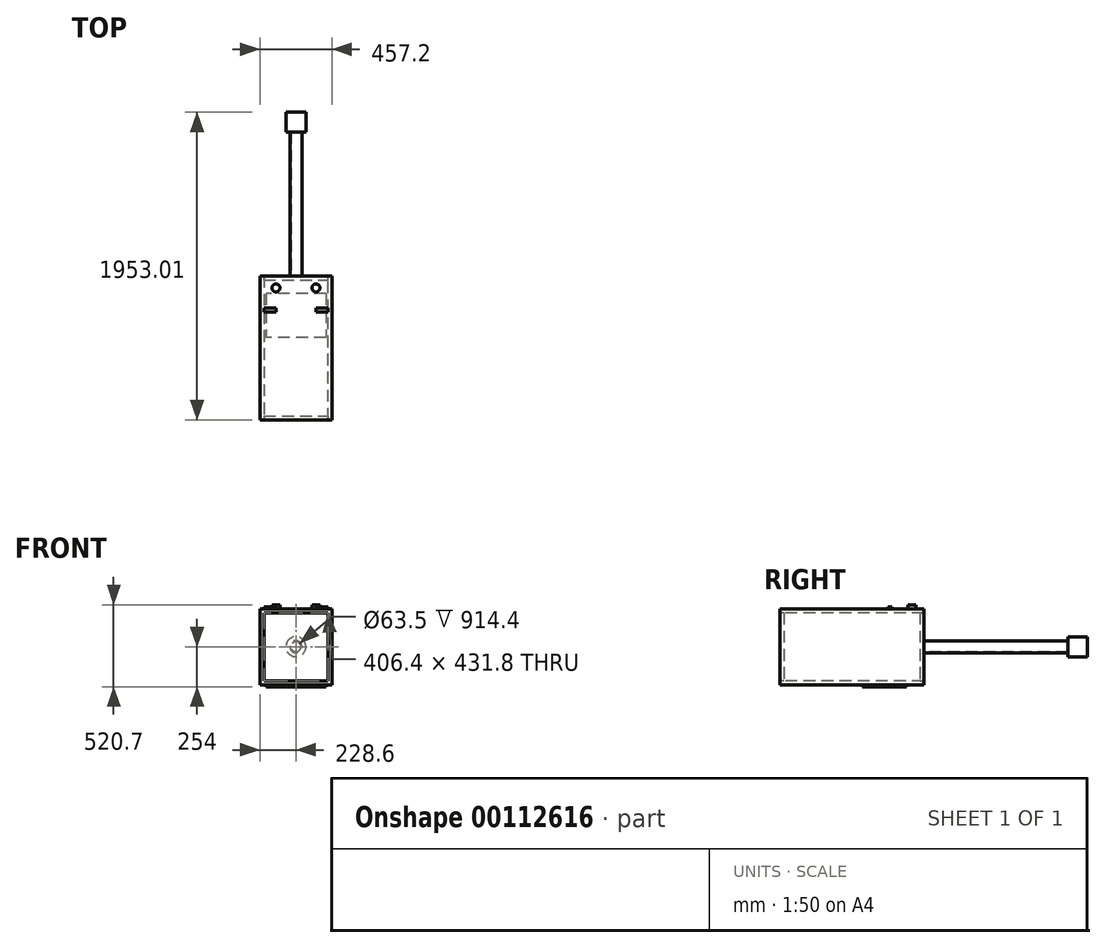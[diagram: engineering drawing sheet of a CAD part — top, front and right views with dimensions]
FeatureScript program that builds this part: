
annotation { "Feature Type Name" : "Feature", "Feature Type Description" : "" }
export const myFeature = defineFeature(function(context is Context, id is Id, definition is map)
    precondition{}
    {
        {
            var Q0;
            Q0=qCreatedBy(makeId("Top.planeOp"),FACE);
            var sketch = newSketch(context, id + "F0", { "sketchPlane" : qUnion([Q0])});
            skLineSegment(sketch, "E0", {"start": v(-228.6, 0) * mm, "end": v(228.6, 0) * mm});
            skLineSegment(sketch, "E1", {"start": v(228.6, 0) * mm, "end": v(228.6, 914.4) * mm});
            skLineSegment(sketch, "E2", {"start": v(228.6, 914.4) * mm, "end": v(-228.6, 914.4) * mm});
            skLineSegment(sketch, "E3", {"start": v(-228.6, 914.4) * mm, "end": v(-228.6, 0) * mm});
            skPoint(sketch, "E4", {"position": v(228.6, 457.2) * mm});
            skSolve(sketch);
        }
        {
            var Q0;
            Q0=makeQuery(id+"F0.imprint","IMPRINT",FACE,{"disambiguationData":[TD([[makeQuery(id+"F0.imprint","IMPRINT",EDGE,{"derivedFrom":sQuery(id+"F0.wireOp",EDGE,"E0")}),1.0]])]});
            extrude(context, id + "F1", {"entities" : qUnion([Q0]), "depth" : 25.4 * mm});
        }
        {
            var Q0;
            Q0=makeQuery(id+"F1.opExtrude","CAP_FACE",FACE,{"disambiguationData":[OSD([sQuery(id+"F0.wireOp",EDGE,"E0"),sQuery(id+"F0.wireOp",EDGE,"E1"),sQuery(id+"F0.wireOp",EDGE,"E2"),sQuery(id+"F0.wireOp",EDGE,"E3")])],"isStart":false});
            var sketch = newSketch(context, id + "F2", { "sketchPlane" : qUnion([Q0])});
            skLineSegment(sketch, "E5", {"start": v(-228.6, 914.4) * mm, "end": v(-228.6, 0) * mm});
            skLineSegment(sketch, "E6", {"start": v(-203.2, 914.4) * mm, "end": v(-203.2, 0) * mm});
            skLineSegment(sketch, "E7", {"start": v(-228.6, 914.4) * mm, "end": v(-203.2, 914.4) * mm});
            skLineSegment(sketch, "E8", {"start": v(-228.6, 0) * mm, "end": v(-203.2, 0) * mm});
            skSolve(sketch);
        }
        {
            var Q0;
            Q0=makeQuery(id+"F2.imprint","IMPRINT",FACE,{"disambiguationData":[TD([[makeQuery(id+"F2.imprint","IMPRINT",EDGE,{"derivedFrom":sQuery(id+"F2.wireOp",EDGE,"E5")}),1.0]])]});
            extrude(context, id + "F3", {"entities" : qUnion([Q0]), "operationType" : NewBodyOperationType.ADD, "depth" : 457.2 * mm});
        }
        {
            var Q0;
            Q0=makeQuery(id+"F1.opExtrude","CAP_FACE",FACE,{"disambiguationData":[OSD([sQuery(id+"F0.wireOp",EDGE,"E0"),sQuery(id+"F0.wireOp",EDGE,"E1"),sQuery(id+"F0.wireOp",EDGE,"E2"),sQuery(id+"F0.wireOp",EDGE,"E3")])],"isStart":false});
            var sketch = newSketch(context, id + "F4", { "sketchPlane" : qUnion([Q0])});
            skLineSegment(sketch, "E9", {"start": v(228.6, 0) * mm, "end": v(228.6, 914.4) * mm});
            skLineSegment(sketch, "E10", {"start": v(203.2, 0) * mm, "end": v(203.2, 914.4) * mm});
            skLineSegment(sketch, "E11", {"start": v(228.6, 0) * mm, "end": v(203.2, 0) * mm});
            skLineSegment(sketch, "E12", {"start": v(228.6, 914.4) * mm, "end": v(203.2, 914.4) * mm});
            skSolve(sketch);
        }
        {
            var Q0;
            Q0=makeQuery(id+"F4.imprint","IMPRINT",FACE,{"disambiguationData":[TD([[makeQuery(id+"F4.imprint","IMPRINT",EDGE,{"derivedFrom":sQuery(id+"F4.wireOp",EDGE,"E9")}),1.0]])]});
            extrude(context, id + "F5", {"entities" : qUnion([Q0]), "operationType" : NewBodyOperationType.ADD, "depth" : 457.2 * mm});
        }
        {
            var Q0;
            Q0=makeQuery(id+"F5.opExtrude","SWEPT_FACE",FACE,{"disambiguationData":[OSD([sQuery(id+"F4.wireOp",EDGE,"E10")])]});
            var sketch = newSketch(context, id + "F6", { "sketchPlane" : qUnion([Q0])});
            skLineSegment(sketch, "E13", {"start": v(0, 482.6) * mm, "end": v(-914.4, 482.6) * mm});
            skLineSegment(sketch, "E14", {"start": v(-914.4, 482.6) * mm, "end": v(-914.4, 457.2) * mm});
            skLineSegment(sketch, "E15", {"start": v(-914.4, 457.2) * mm, "end": v(0, 457.2) * mm});
            skLineSegment(sketch, "E16", {"start": v(0, 457.2) * mm, "end": v(0, 482.6) * mm});
            skSolve(sketch);
        }
        {
            var Q0;
            Q0 = qSketchRegion(id + "F6", true);
            extrude(context, id + "F7", {"entities" : qUnion([Q0]), "operationType" : NewBodyOperationType.ADD, "depth" : 431.8 * mm});
        }
        {
            var Q0;
            Q0=makeQuery(id+"F7.boolean.opBoolean","MERGE",FACE,{"derivedFrom":[makeQuery(id+"F5.boolean.opBoolean","MERGE",FACE,{"derivedFrom":[makeQuery(id+"F3.boolean.opBoolean","MERGE",FACE,{"derivedFrom":[makeQuery(id+"F1.opExtrude","SWEPT_FACE",FACE,{"disambiguationData":[OSD([sQuery(id+"F0.wireOp",EDGE,"E0")])]}),makeQuery(id+"F3.opExtrude","SWEPT_FACE",FACE,{"disambiguationData":[OSD([sQuery(id+"F2.wireOp",EDGE,"E8")])]})]}),makeQuery(id+"F5.opExtrude","SWEPT_FACE",FACE,{"disambiguationData":[OSD([sQuery(id+"F4.wireOp",EDGE,"E11")])]})]}),makeQuery(id+"F7.opExtrude","SWEPT_FACE",FACE,{"disambiguationData":[OSD([sQuery(id+"F6.wireOp",EDGE,"E16")])]})]});
            var sketch = newSketch(context, id + "F8", { "sketchPlane" : qUnion([Q0])});
            skLineSegment(sketch, "E17", {"start": v(-203.2, 457.2) * mm, "end": v(203.2, 457.2) * mm});
            skLineSegment(sketch, "E18", {"start": v(203.2, 457.2) * mm, "end": v(203.2, 25.4) * mm});
            skLineSegment(sketch, "E19", {"start": v(203.2, 25.4) * mm, "end": v(-203.2, 25.4) * mm});
            skLineSegment(sketch, "E20", {"start": v(-203.2, 25.4) * mm, "end": v(-203.2, 457.2) * mm});
            skSolve(sketch);
        }
        {
            var Q0;
            Q0 = qSketchRegion(id + "F8", true);
            extrude(context, id + "F9", {"entities" : qUnion([Q0]), "oppositeDirection" : true, "depth" : 25.4 * mm});
        }
        {
            var Q0;
            Q0=makeQuery(id+"F7.boolean.opBoolean","MERGE",FACE,{"derivedFrom":[makeQuery(id+"F5.boolean.opBoolean","MERGE",FACE,{"derivedFrom":[makeQuery(id+"F3.boolean.opBoolean","MERGE",FACE,{"derivedFrom":[makeQuery(id+"F1.opExtrude","SWEPT_FACE",FACE,{"disambiguationData":[OSD([sQuery(id+"F0.wireOp",EDGE,"E2")])]}),makeQuery(id+"F3.opExtrude","SWEPT_FACE",FACE,{"disambiguationData":[OSD([sQuery(id+"F2.wireOp",EDGE,"E7")])]})]}),makeQuery(id+"F5.opExtrude","SWEPT_FACE",FACE,{"disambiguationData":[OSD([sQuery(id+"F4.wireOp",EDGE,"E12")])]})]}),makeQuery(id+"F7.opExtrude","SWEPT_FACE",FACE,{"disambiguationData":[OSD([sQuery(id+"F6.wireOp",EDGE,"E14")])]})]});
            var sketch = newSketch(context, id + "F10", { "sketchPlane" : qUnion([Q0])});
            skLineSegment(sketch, "E21", {"start": v(-203.2, 457.2) * mm, "end": v(203.2, 457.2) * mm});
            skLineSegment(sketch, "E22", {"start": v(203.2, 457.2) * mm, "end": v(203.2, 25.4) * mm});
            skLineSegment(sketch, "E23", {"start": v(203.2, 25.4) * mm, "end": v(-203.2, 25.4) * mm});
            skLineSegment(sketch, "E24", {"start": v(-203.2, 25.4) * mm, "end": v(-203.2, 457.2) * mm});
            skSolve(sketch);
        }
        {
            var Q0;
            Q0 = qSketchRegion(id + "F10", true);
            extrude(context, id + "F11", {"entities" : qUnion([Q0]), "oppositeDirection" : true, "depth" : 25.4 * mm});
        }
        {
            var Q0;
            Q0=makeQuery(id+"F7.boolean.opBoolean","MERGE",FACE,{"derivedFrom":[makeQuery(id+"F3.opExtrude","CAP_FACE",FACE,{"disambiguationData":[OSD([sQuery(id+"F2.wireOp",EDGE,"E5"),sQuery(id+"F2.wireOp",EDGE,"E6"),sQuery(id+"F2.wireOp",EDGE,"E7"),sQuery(id+"F2.wireOp",EDGE,"E8")])],"isStart":false}),makeQuery(id+"F5.opExtrude","CAP_FACE",FACE,{"disambiguationData":[OSD([sQuery(id+"F4.wireOp",EDGE,"E9"),sQuery(id+"F4.wireOp",EDGE,"E10"),sQuery(id+"F4.wireOp",EDGE,"E11"),sQuery(id+"F4.wireOp",EDGE,"E12")])],"isStart":false}),makeQuery(id+"F7.opExtrude","SWEPT_FACE",FACE,{"disambiguationData":[OSD([sQuery(id+"F6.wireOp",EDGE,"E13")])]})]});
            var sketch = newSketch(context, id + "F12", { "sketchPlane" : qUnion([Q0])});
            skPoint(sketch, "E25", {"position": v(-228.6, 710.12) * mm});
            skPoint(sketch, "E26", {"position": v(228.6, 710.12) * mm});
            skPoint(sketch, "E27", {"position": v(-228.6, 601.68) * mm});
            skPoint(sketch, "E28", {"position": v(228.6, 601.68) * mm});
            skLineSegment(sketch, "E29", {"start": v(-228.6, 710.12) * mm, "end": v(228.6, 710.12) * mm, "construction": true});
            skLineSegment(sketch, "E30", {"start": v(-228.6, 601.68) * mm, "end": v(228.6, 601.68) * mm, "construction": true});
            skPoint(sketch, "E31", {"position": v(0, 601.68) * mm});
            skLineSegment(sketch, "E32", {"start": v(0, 601.68) * mm, "end": v(0, 855.68) * mm, "construction": true});
            skPoint(sketch, "E32.endSnap0", {"position": v(0, 914.4) * mm});
            skLineSegment(sketch, "E33.bottom", {"start": v(-203.2, 710.12) * mm, "end": v(-127, 710.12) * mm});
            skLineSegment(sketch, "E33.top", {"start": v(-203.2, 684.72) * mm, "end": v(-127, 684.72) * mm});
            skLineSegment(sketch, "E33.left", {"start": v(-203.2, 710.12) * mm, "end": v(-203.2, 684.72) * mm});
            skLineSegment(sketch, "E33.right", {"start": v(-127, 710.12) * mm, "end": v(-127, 684.72) * mm});
            skLineSegment(sketch, "E34.bottom", {"start": v(203.2, 710.12) * mm, "end": v(127, 710.12) * mm});
            skLineSegment(sketch, "E34.top", {"start": v(203.2, 684.72) * mm, "end": v(127, 684.72) * mm});
            skLineSegment(sketch, "E34.left", {"start": v(203.2, 710.12) * mm, "end": v(203.2, 684.72) * mm});
            skLineSegment(sketch, "E34.right", {"start": v(127, 710.12) * mm, "end": v(127, 684.72) * mm});
            skLineSegment(sketch, "E35", {"start": v(-228.6, 710.12) * mm, "end": v(-228.6, 837.12) * mm, "construction": true});
            skLineSegment(sketch, "E36", {"start": v(228.6, 710.12) * mm, "end": v(228.6, 837.12) * mm, "construction": true});
            skLineSegment(sketch, "E37", {"start": v(-228.6, 837.12) * mm, "end": v(-127, 837.12) * mm, "construction": true});
            skLineSegment(sketch, "E38", {"start": v(228.6, 837.12) * mm, "end": v(127, 837.12) * mm, "construction": true});
            skCircle(sketch, "E39", {"center": v(-127, 837.12) * mm, "radius": 25.4 * mm});
            skCircle(sketch, "E40", {"center": v(127, 837.12) * mm, "radius": 25.4 * mm});
            skSolve(sketch);
        }
        {
            var Q0;
            Q0=makeQuery(id+"F12.imprint","IMPRINT",FACE,{"disambiguationData":[TD([[makeQuery(id+"F12.imprint","IMPRINT",EDGE,{"derivedFrom":sQuery(id+"F12.wireOp",EDGE,"E40")}),1.0]])]});
            var Q1;
            Q1=makeQuery(id+"F12.imprint","IMPRINT",FACE,{"disambiguationData":[TD([[makeQuery(id+"F12.imprint","IMPRINT",EDGE,{"derivedFrom":sQuery(id+"F12.wireOp",EDGE,"E39")}),1.0]])]});
            extrude(context, id + "F13", {"entities" : qUnion([Q0, Q1]), "operationType" : NewBodyOperationType.ADD, "depth" : 25.4 * mm});
        }
        {
            var Q0;
            Q0=makeQuery(id+"F12.imprint","IMPRINT",FACE,{"disambiguationData":[TD([[makeQuery(id+"F12.imprint","IMPRINT",EDGE,{"derivedFrom":sQuery(id+"F12.wireOp",EDGE,"E33.bottom")}),-1.0]])]});
            var Q1;
            Q1=makeQuery(id+"F12.imprint","IMPRINT",FACE,{"disambiguationData":[TD([[makeQuery(id+"F12.imprint","IMPRINT",EDGE,{"derivedFrom":sQuery(id+"F12.wireOp",EDGE,"E34.bottom")}),1.0]])]});
            extrude(context, id + "F14", {"entities" : qUnion([Q0, Q1]), "operationType" : NewBodyOperationType.ADD, "depth" : 12.7 * mm});
        }
        {
            var Q0;
            Q0=makeQuery(id+"F1.opExtrude","CAP_FACE",FACE,{"disambiguationData":[OSD([sQuery(id+"F0.wireOp",EDGE,"E0"),sQuery(id+"F0.wireOp",EDGE,"E1"),sQuery(id+"F0.wireOp",EDGE,"E2"),sQuery(id+"F0.wireOp",EDGE,"E3")])],"isStart":true});
            var sketch = newSketch(context, id + "F15", { "sketchPlane" : qUnion([Q0])});
            skPoint(sketch, "E41", {"position": v(228.6, -803.17) * mm});
            skPoint(sketch, "E42", {"position": v(-228.6, -803.17) * mm});
            skPoint(sketch, "E43", {"position": v(-228.6, -523.16) * mm});
            skPoint(sketch, "E44", {"position": v(228.6, -523.16) * mm});
            skLineSegment(sketch, "E45", {"start": v(228.6, -803.17) * mm, "end": v(-228.6, -803.17) * mm, "construction": true});
            skLineSegment(sketch, "E46", {"start": v(228.6, -523.16) * mm, "end": v(-228.6, -523.16) * mm, "construction": true});
            skLineSegment(sketch, "E47", {"start": v(228.6, -803.17) * mm, "end": v(228.6, -523.16) * mm, "construction": true});
            skLineSegment(sketch, "E48", {"start": v(-228.6, -803.17) * mm, "end": v(-228.6, -523.16) * mm, "construction": true});
            skPoint(sketch, "E49", {"position": v(0, -803.17) * mm});
            skPoint(sketch, "E50", {"position": v(0, -523.16) * mm});
            skLineSegment(sketch, "E51", {"start": v(-190.5, -803.17) * mm, "end": v(-190.5, -523.16) * mm});
            skLineSegment(sketch, "E52", {"start": v(190.5, -803.17) * mm, "end": v(190.5, -523.16) * mm});
            skLineSegment(sketch, "E53", {"start": v(190.5, -803.17) * mm, "end": v(-190.5, -803.17) * mm});
            skLineSegment(sketch, "E54", {"start": v(190.5, -523.16) * mm, "end": v(-190.5, -523.16) * mm});
            skSolve(sketch);
        }
        {
            var Q0;
            Q0=makeQuery(id+"F15.imprint","IMPRINT",FACE,{"disambiguationData":[TD([[makeQuery(id+"F15.imprint","IMPRINT",EDGE,{"derivedFrom":sQuery(id+"F15.wireOp",EDGE,"E51")}),-1.0]])]});
            extrude(context, id + "F16", {"entities" : qUnion([Q0]), "operationType" : NewBodyOperationType.ADD, "depth" : 12.7 * mm});
        }
        {
            var Q0;
            Q0=makeQuery(id+"F11.opExtrude","CAP_FACE",FACE,{"disambiguationData":[OSD([sQuery(id+"F10.wireOp",EDGE,"E21"),sQuery(id+"F10.wireOp",EDGE,"E22"),sQuery(id+"F10.wireOp",EDGE,"E23"),sQuery(id+"F10.wireOp",EDGE,"E24")])],"isStart":true});
            var sketch = newSketch(context, id + "F17", { "sketchPlane" : qUnion([Q0])});
            skPoint(sketch, "E55", {"position": v(203.2, 25.4) * mm});
            skPoint(sketch, "E56", {"position": v(-203.2, 25.4) * mm});
            skPoint(sketch, "E57", {"position": v(-203.2, 457.2) * mm});
            skPoint(sketch, "E58", {"position": v(203.2, 457.2) * mm});
            skLineSegment(sketch, "E59", {"start": v(203.2, 25.4) * mm, "end": v(203.2, 457.2) * mm, "construction": true});
            skLineSegment(sketch, "E60", {"start": v(203.2, 457.2) * mm, "end": v(-203.2, 457.2) * mm, "construction": true});
            skLineSegment(sketch, "E61", {"start": v(-203.2, 457.2) * mm, "end": v(-203.2, 25.4) * mm, "construction": true});
            skLineSegment(sketch, "E62", {"start": v(-203.2, 25.4) * mm, "end": v(203.2, 25.4) * mm, "construction": true});
            skPoint(sketch, "E63", {"position": v(203.2, 241.3) * mm});
            skPoint(sketch, "E64", {"position": v(0, 25.4) * mm});
            skPoint(sketch, "E65", {"position": v(-203.2, 241.3) * mm});
            skLineSegment(sketch, "E66", {"start": v(0, 25.4) * mm, "end": v(0, 457.2) * mm, "construction": true});
            skLineSegment(sketch, "E67", {"start": v(203.2, 241.3) * mm, "end": v(-203.2, 241.3) * mm, "construction": true});
            skPoint(sketch, "E68", {"position": v(0, 241.3) * mm});
            skCircle(sketch, "E69", {"center": v(0, 241.3) * mm, "radius": 38.1 * mm});
            skCircle(sketch, "E70", {"center": v(0, 241.3) * mm, "radius": 31.75 * mm});
            skSolve(sketch);
        }
        {
            var Q0;
            Q0=makeQuery(id+"F17.imprint","IMPRINT",FACE,{"disambiguationData":[TD([[makeQuery(id+"F17.imprint","IMPRINT",EDGE,{"derivedFrom":sQuery(id+"F17.wireOp",EDGE,"E69")}),1.0]])]});
            extrude(context, id + "F18", {"entities" : qUnion([Q0]), "operationType" : NewBodyOperationType.ADD, "depth" : 914.4 * mm});
        }
        {
            var Q0;
            Q0=makeQuery(id+"F18.opExtrude","CAP_FACE",FACE,{"disambiguationData":[OSD([sQuery(id+"F17.wireOp",EDGE,"E69"),sQuery(id+"F17.wireOp",EDGE,"E70")])],"isStart":false});
            var sketch = newSketch(context, id + "F19", { "sketchPlane" : qUnion([Q0])});
            skCircle(sketch, "E71", {"center": v(0, 241.3) * mm, "radius": 63.5 * mm});
            skSolve(sketch);
        }
        {
            var Q0;
            Q0=makeQuery(id+"F19.imprint","IMPRINT",FACE,{"disambiguationData":[TD([[makeQuery(id+"F19.imprint","IMPRINT",EDGE,{"derivedFrom":makeQuery(id+"F18.opExtrude","CAP_EDGE",EDGE,{"disambiguationData":[OSD([sQuery(id+"F17.wireOp",EDGE,"E70")])],"isStart":false})}),1.0]])]});
            var Q1;
            Q1=makeQuery(id+"F19.imprint","IMPRINT",FACE,{"disambiguationData":[TD([[makeQuery(id+"F19.imprint","IMPRINT",EDGE,{"derivedFrom":makeQuery(id+"F18.opExtrude","CAP_EDGE",EDGE,{"disambiguationData":[OSD([sQuery(id+"F17.wireOp",EDGE,"E69")])],"isStart":false})}),1.0]])]});
            var Q2;
            Q2=makeQuery(id+"F19.imprint","IMPRINT",FACE,{"disambiguationData":[TD([[makeQuery(id+"F19.imprint","IMPRINT",EDGE,{"derivedFrom":sQuery(id+"F19.wireOp",EDGE,"E71")}),1.0]])]});
            extrude(context, id + "F20", {"entities" : qUnion([Q0, Q1, Q2]), "operationType" : NewBodyOperationType.ADD, "depth" : 124.2 * mm});
        }
    });
